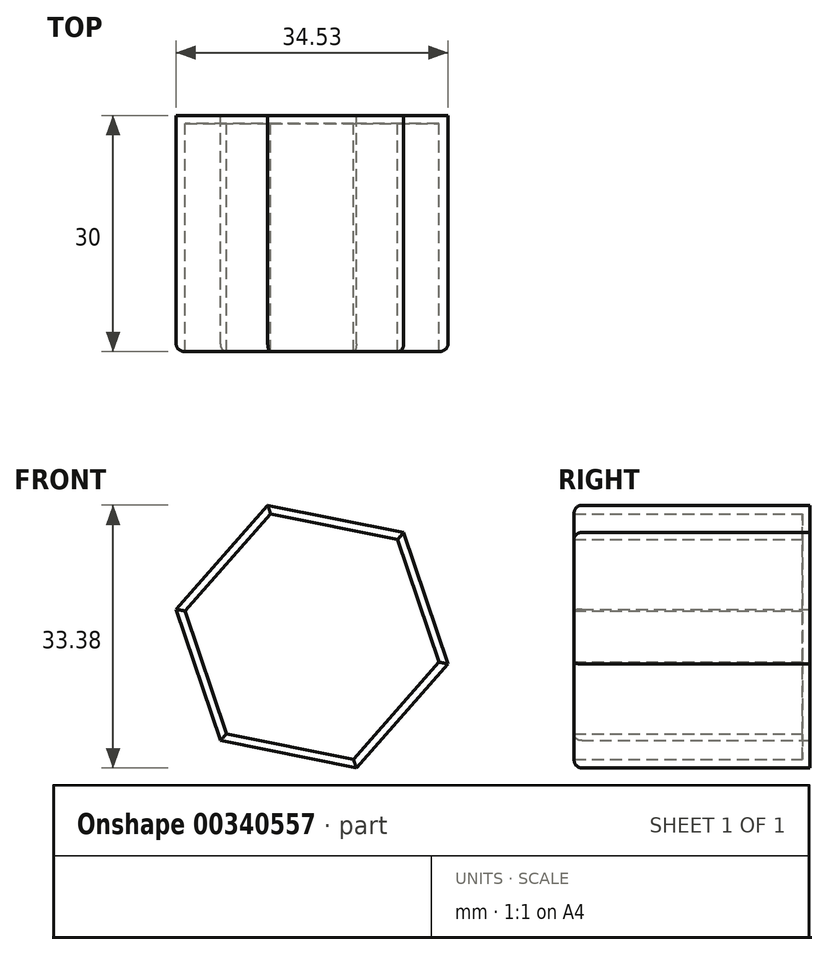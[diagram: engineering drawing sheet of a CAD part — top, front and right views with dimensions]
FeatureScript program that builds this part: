
annotation { "Feature Type Name" : "Feature", "Feature Type Description" : "" }
export const myFeature = defineFeature(function(context is Context, id is Id, definition is map)
    precondition{}
    {
        {
            var Q0;
            Q0=qCreatedBy(makeId("Front.planeOp"),FACE);
            var sketch = newSketch(context, id + "F0", { "sketchPlane" : qUnion([Q0])});
            skCircle(sketch, "E0.cCircle", {"center": v(-21.7, 27) * mm, "radius": 15.25 * mm, "construction": true});
            skLineSegment(sketch, "E0.0", {"start": v(-4.43, 23.52) * mm, "end": v(-16.07, 10.3) * mm});
            skLineSegment(sketch, "E0.1", {"start": v(-16.07, 10.3) * mm, "end": v(-33.33, 13.77) * mm});
            skLineSegment(sketch, "E0.2", {"start": v(-33.33, 13.77) * mm, "end": v(-38.96, 30.46) * mm});
            skLineSegment(sketch, "E0.3", {"start": v(-38.96, 30.46) * mm, "end": v(-27.32, 43.68) * mm});
            skLineSegment(sketch, "E0.4", {"start": v(-27.32, 43.68) * mm, "end": v(-10.06, 40.2) * mm});
            skLineSegment(sketch, "E0.5", {"start": v(-10.06, 40.2) * mm, "end": v(-4.43, 23.52) * mm});
            skPoint(sketch, "E0.0.midPoint", {"position": v(-10.25, 16.91) * mm});
            skSolve(sketch);
        }
        {
            var Q0;
            Q0=makeQuery(id+"F0.imprint","IMPRINT",FACE,{"disambiguationData":[TD([[makeQuery(id+"F0.imprint","IMPRINT",EDGE,{"derivedFrom":sQuery(id+"F0.wireOp",EDGE,"E0.0")}),-1.0]])]});
            extrude(context, id + "F1", {"entities" : qUnion([Q0]), "depth" : 30 * mm});
        }
        {
            var Q0;
            Q0=makeQuery(id+"F1.opExtrude","CAP_FACE",FACE,{"disambiguationData":[OSD([sQuery(id+"F0.wireOp",EDGE,"E0.0"),sQuery(id+"F0.wireOp",EDGE,"E0.1"),sQuery(id+"F0.wireOp",EDGE,"E0.2"),sQuery(id+"F0.wireOp",EDGE,"E0.3"),sQuery(id+"F0.wireOp",EDGE,"E0.4"),sQuery(id+"F0.wireOp",EDGE,"E0.5")])],"isStart":false});
            shell(context, id + "F2", {"entities" : qUnion([Q0]), "thickness" : 1 * mm});
        }
        {
            var Q0;
            Q0=makeQuery(id+"F1.opExtrude","CAP_EDGE",EDGE,{"disambiguationData":[OSD([sQuery(id+"F0.wireOp",EDGE,"E0.4")])],"isStart":false});
            var Q1;
            Q1=makeQuery(id+"F1.opExtrude","CAP_EDGE",EDGE,{"disambiguationData":[OSD([sQuery(id+"F0.wireOp",EDGE,"E0.5")])],"isStart":false});
            var Q2;
            Q2=makeQuery(id+"F1.opExtrude","CAP_EDGE",EDGE,{"disambiguationData":[OSD([sQuery(id+"F0.wireOp",EDGE,"E0.0")])],"isStart":false});
            var Q3;
            Q3=makeQuery(id+"F1.opExtrude","CAP_EDGE",EDGE,{"disambiguationData":[OSD([sQuery(id+"F0.wireOp",EDGE,"E0.1")])],"isStart":false});
            var Q4;
            Q4=makeQuery(id+"F1.opExtrude","CAP_EDGE",EDGE,{"disambiguationData":[OSD([sQuery(id+"F0.wireOp",EDGE,"E0.2")])],"isStart":false});
            var Q5;
            Q5=makeQuery(id+"F1.opExtrude","CAP_EDGE",EDGE,{"disambiguationData":[OSD([sQuery(id+"F0.wireOp",EDGE,"E0.3")])],"isStart":false});
            fillet(context, id + "F3", {"entities" : qUnion([Q0, Q1, Q2, Q3, Q4, Q5]), "radius" : 1 * mm, "tangentPropagation" : true, "allowEdgeOverflow" : false});
        }
    });
